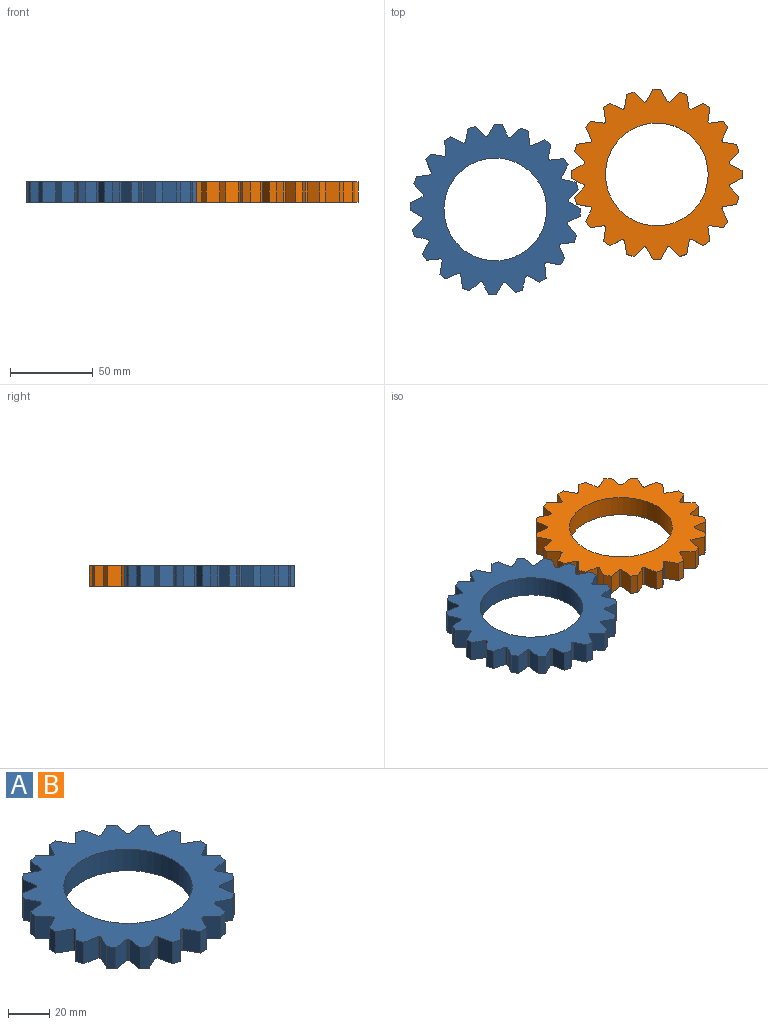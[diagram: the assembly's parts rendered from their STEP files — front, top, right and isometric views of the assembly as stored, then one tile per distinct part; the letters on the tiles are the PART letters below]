
ASSEMBLY  parts=2 mates=1
PART A: 83 faces, bbox 103.2x103.2x12.7 mm
  f0: plane 12.7x7.62mm, normal (0.47,0.88,0), area 109.7mm2, adj f1,f79,f81,f82
  f1: cylinder r=44.45mm len=12.7mm, axis (0,0,-1), area 15.5mm2, adj f0,f2,f81,f82
  f2: plane 12.7x6.21mm, normal (0.72,-0.69,0), area 109.6mm2, adj f1,f3,f81,f82
  f3: plane 12.7x4.35mm, normal (0.95,0.31,0), area 58.1mm2, adj f2,f4,f81,f82
  f4: plane 12.7x8.51mm, normal (0.18,0.98,0), area 109.7mm2, adj f3,f5,f81,f82
  f5: cylinder r=44.45mm len=12.7mm, axis (0,0,-1), area 15.5mm2, adj f4,f6,f81,f82
  f6: plane 12.7x7.76mm, normal (0.9,-0.44,0), area 109.6mm2, adj f5,f7,f81,f82
  f7: plane 12.7x3.7mm, normal (0.81,0.59,0), area 58.1mm2, adj f6,f8,f81,f82
  f8: plane 12.7x8.56mm, normal (-0.14,0.99,0), area 109.7mm2, adj f7,f9,f81,f82
  f9: cylinder r=44.45mm len=12.7mm, axis (0,0,-1), area 15.5mm2, adj f8,f10,f81,f82
  f10: plane 12.7x8.55mm, normal (0.99,-0.14,0), area 109.6mm2, adj f9,f11,f81,f82
  f11: plane 12.7x3.7mm, normal (0.59,0.81,0), area 58.1mm2, adj f10,f12,f81,f82
  f12: plane 12.7x7.77mm, normal (-0.44,0.9,0), area 109.7mm2, adj f11,f13,f81,f82
  f13: cylinder r=44.45mm len=12.7mm, axis (0,0,-1), area 15.5mm2, adj f12,f14,f81,f82
  f14: plane 12.7x8.5mm, normal (0.98,0.17,0), area 109.6mm2, adj f13,f15,f81,f82
  f15: plane 12.7x4.35mm, normal (0.31,0.95,0), area 58.1mm2, adj f14,f16,f81,f82
  f16: plane 12.7x6.23mm, normal (-0.69,0.72,0), area 109.7mm2, adj f15,f17,f81,f82
  f17: cylinder r=44.45mm len=12.7mm, axis (0,0,-1), area 15.5mm2, adj f16,f18,f81,f82
  f18: plane 12.7x7.62mm, normal (0.88,0.47,0), area 109.6mm2, adj f17,f19,f81,f82
  f19: plane 12.7x4.57mm, normal (0,1,0), area 58.1mm2, adj f18,f20,f81,f82
  f20: plane 12.7x7.62mm, normal (-0.88,0.47,0), area 109.7mm2, adj f19,f21,f81,f82
  f21: cylinder r=44.45mm len=12.7mm, axis (0,0,-1), area 15.5mm2, adj f20,f22,f81,f82
  f22: plane 12.7x6.21mm, normal (0.69,0.72,0), area 109.6mm2, adj f21,f23,f81,f82
  f23: plane 12.7x4.35mm, normal (-0.31,0.95,0), area 58.1mm2, adj f22,f24,f81,f82
  f24: plane 12.7x8.51mm, normal (-0.98,0.18,0), area 109.7mm2, adj f23,f25,f81,f82
  f25: cylinder r=44.45mm len=12.7mm, axis (0,0,-1), area 15.5mm2, adj f24,f26,f81,f82
  f26: plane 12.7x7.76mm, normal (0.44,0.9,0), area 109.6mm2, adj f25,f27,f81,f82
  f27: plane 12.7x3.7mm, normal (-0.59,0.81,0), area 58.1mm2, adj f26,f28,f81,f82
  f28: plane 12.7x8.56mm, normal (-0.99,-0.14,0), area 109.7mm2, adj f27,f29,f81,f82
  f29: cylinder r=44.45mm len=12.7mm, axis (0,0,-1), area 15.5mm2, adj f28,f30,f81,f82
  f30: plane 12.7x8.55mm, normal (0.14,0.99,0), area 109.6mm2, adj f29,f31,f81,f82
  f31: plane 12.7x3.7mm, normal (-0.81,0.59,0), area 58.1mm2, adj f30,f32,f81,f82
  f32: plane 12.7x7.77mm, normal (-0.9,-0.44,0), area 109.7mm2, adj f31,f33,f81,f82
  f33: cylinder r=44.45mm len=12.7mm, axis (0,0,-1), area 15.5mm2, adj f32,f34,f81,f82
  f34: plane 12.7x8.5mm, normal (-0.17,0.98,0), area 109.6mm2, adj f33,f35,f81,f82
  f35: plane 12.7x4.35mm, normal (-0.95,0.31,0), area 58.1mm2, adj f34,f36,f81,f82
  f36: plane 12.7x6.23mm, normal (-0.72,-0.69,0), area 109.7mm2, adj f35,f37,f81,f82
  f37: cylinder r=44.45mm len=12.7mm, axis (0,0,-1), area 15.5mm2, adj f36,f38,f81,f82
  f38: plane 12.7x7.62mm, normal (-0.47,0.88,0), area 109.6mm2, adj f37,f39,f81,f82
  f39: plane 12.7x4.57mm, normal (-1,0,0), area 58.1mm2, adj f38,f40,f81,f82
  f40: plane 12.7x7.62mm, normal (-0.47,-0.88,0), area 109.7mm2, adj f39,f41,f81,f82
  f41: cylinder r=44.45mm len=12.7mm, axis (0,0,-1), area 15.5mm2, adj f40,f42,f81,f82
  f42: plane 12.7x6.21mm, normal (-0.72,0.69,0), area 109.6mm2, adj f41,f43,f81,f82
  f43: plane 12.7x4.35mm, normal (-0.95,-0.31,0), area 58.1mm2, adj f42,f44,f81,f82
  f44: plane 12.7x8.51mm, normal (-0.18,-0.98,0), area 109.7mm2, adj f43,f45,f81,f82
  f45: cylinder r=44.45mm len=12.7mm, axis (0,0,-1), area 15.5mm2, adj f44,f46,f81,f82
  f46: plane 12.7x7.76mm, normal (-0.9,0.44,0), area 109.6mm2, adj f45,f47,f81,f82
  f47: plane 12.7x3.7mm, normal (-0.81,-0.59,0), area 58.1mm2, adj f46,f48,f81,f82
  f48: plane 12.7x8.56mm, normal (0.14,-0.99,0), area 109.7mm2, adj f47,f49,f81,f82
  f49: cylinder r=44.45mm len=12.7mm, axis (0,0,-1), area 15.5mm2, adj f48,f50,f81,f82
  f50: plane 12.7x8.55mm, normal (-0.99,0.14,0), area 109.6mm2, adj f49,f51,f81,f82
  f51: plane 12.7x3.7mm, normal (-0.59,-0.81,0), area 58.1mm2, adj f50,f52,f81,f82
  f52: plane 12.7x7.77mm, normal (0.44,-0.9,0), area 109.7mm2, adj f51,f53,f81,f82
  f53: cylinder r=44.45mm len=12.7mm, axis (0,0,-1), area 15.5mm2, adj f52,f54,f81,f82
  f54: plane 12.7x8.5mm, normal (-0.98,-0.17,0), area 109.6mm2, adj f53,f55,f81,f82
  f55: plane 12.7x4.35mm, normal (-0.31,-0.95,0), area 58.1mm2, adj f54,f56,f81,f82
  f56: plane 12.7x6.23mm, normal (0.69,-0.72,0), area 109.7mm2, adj f55,f57,f81,f82
  f57: cylinder r=44.45mm len=12.7mm, axis (0,0,-1), area 15.5mm2, adj f56,f58,f81,f82
  f58: plane 12.7x7.62mm, normal (-0.88,-0.47,0), area 109.6mm2, adj f57,f59,f81,f82
  f59: plane 12.7x4.57mm, normal (0,-1,0), area 58.1mm2, adj f58,f60,f81,f82
  f60: plane 12.7x7.62mm, normal (0.88,-0.47,0), area 109.7mm2, adj f59,f61,f81,f82
  f61: cylinder r=44.45mm len=12.7mm, axis (0,0,-1), area 15.5mm2, adj f60,f62,f81,f82
  f62: plane 12.7x6.21mm, normal (-0.69,-0.72,0), area 109.6mm2, adj f61,f63,f81,f82
  f63: plane 12.7x4.35mm, normal (0.31,-0.95,0), area 58.1mm2, adj f62,f64,f81,f82
  f64: plane 12.7x8.51mm, normal (0.98,-0.18,0), area 109.7mm2, adj f63,f65,f81,f82
  f65: cylinder r=44.45mm len=12.7mm, axis (0,0,-1), area 15.5mm2, adj f64,f66,f81,f82
  f66: plane 12.7x7.76mm, normal (-0.44,-0.9,0), area 109.6mm2, adj f65,f67,f81,f82
  f67: plane 12.7x3.7mm, normal (0.59,-0.81,0), area 58.1mm2, adj f66,f68,f81,f82
  f68: plane 12.7x8.56mm, normal (0.99,0.14,0), area 109.7mm2, adj f67,f69,f81,f82
  f69: cylinder r=44.45mm len=12.7mm, axis (0,0,-1), area 15.5mm2, adj f68,f70,f81,f82
  f70: plane 12.7x8.55mm, normal (-0.14,-0.99,0), area 109.6mm2, adj f69,f71,f81,f82
  f71: plane 12.7x3.7mm, normal (0.81,-0.59,0), area 58.1mm2, adj f70,f72,f81,f82
  f72: plane 12.7x7.77mm, normal (0.9,0.44,0), area 109.7mm2, adj f71,f73,f81,f82
  f73: cylinder r=44.45mm len=12.7mm, axis (0,0,-1), area 15.5mm2, adj f72,f74,f81,f82
  f74: plane 12.7x8.5mm, normal (0.17,-0.98,0), area 109.6mm2, adj f73,f75,f81,f82
  f75: plane 12.7x4.35mm, normal (0.95,-0.31,0), area 58.1mm2, adj f74,f76,f81,f82
  f76: plane 12.7x6.23mm, normal (0.72,0.69,0), area 109.7mm2, adj f75,f77,f81,f82
  f77: cylinder r=44.45mm len=12.7mm, axis (0,0,-1), area 15.5mm2, adj f76,f78,f81,f82
  f78: plane 12.7x7.62mm, normal (0.47,-0.88,0), area 109.6mm2, adj f77,f79,f81,f82
  f79: plane 12.7x4.57mm, normal (1,0,0), area 58.1mm2, adj f0,f78,f81,f82
  f80: cylinder r=31.12mm len=62.23mm, axis (0,0,-1), area 2482.9mm2, adj f81,f82
  f81: plane 103.22x103.22mm, normal (0,0,1), area 4404.2mm2, adj f0,f1,f2,f3,f4,f5,f6,f7
  f82: plane 103.22x103.22mm, normal (0,0,-1), area 4404.2mm2, adj f0,f1,f2,f3,f4,f5,f6,f7
PART B: same geometry as A
PLACE A rot(axis=(0,0,-1),20deg) t=(-97.14,-20.96,-6.37)mm
PLACE B t=(0.65,0.23,-6.37)mm
MATE parallel A.f81 <-> B.f80  axis (0,0,1) through (-65.06,9.8,6.33)mm
